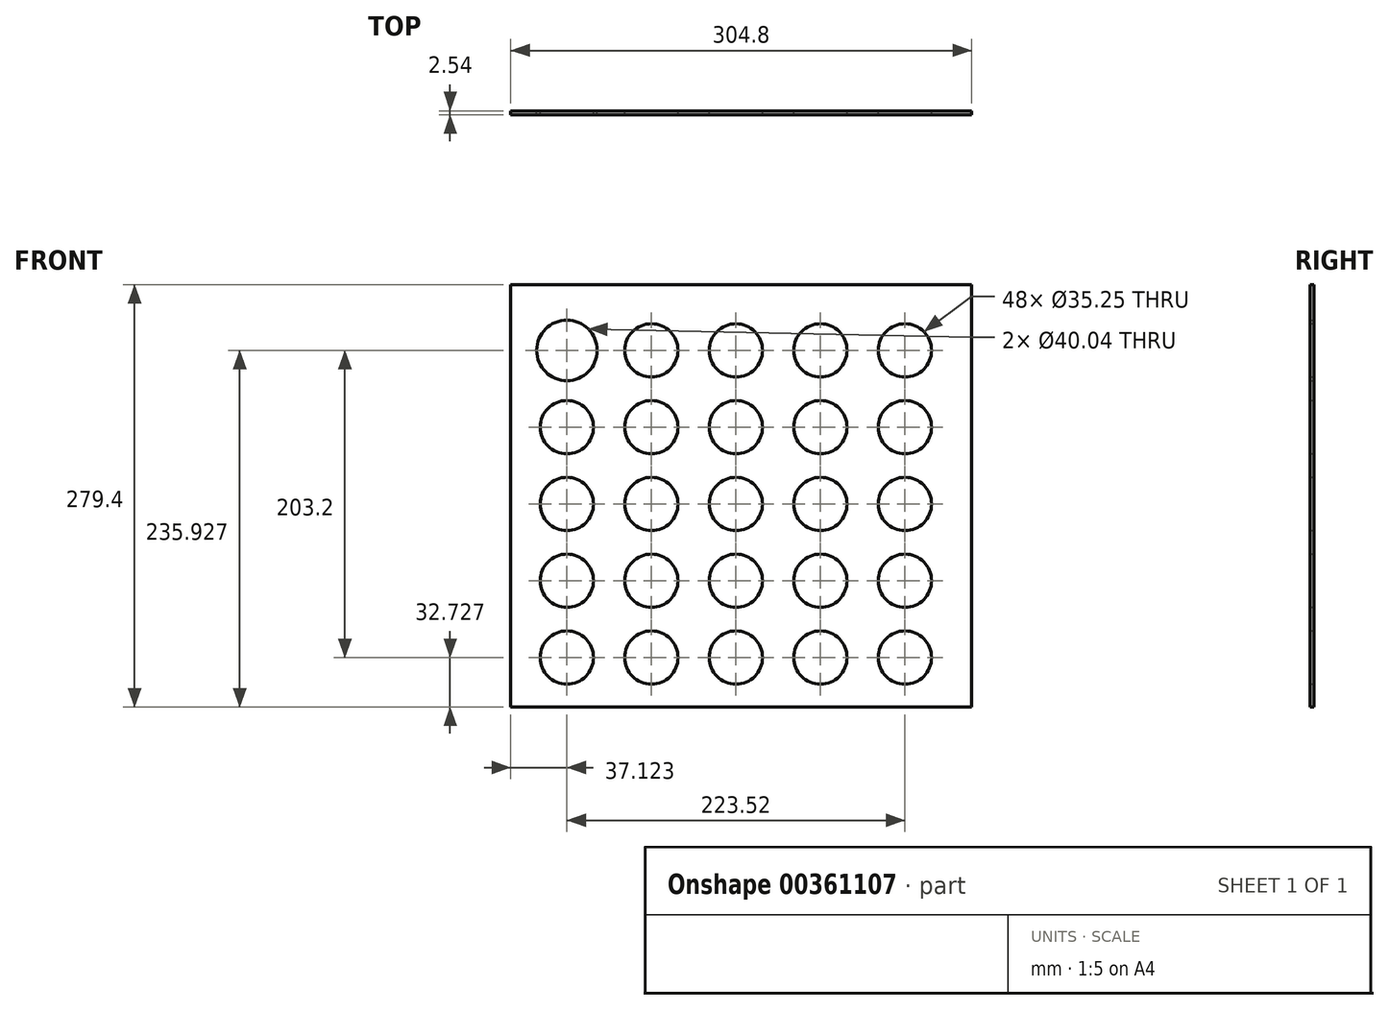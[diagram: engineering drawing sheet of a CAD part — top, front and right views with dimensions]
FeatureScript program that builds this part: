
annotation { "Feature Type Name" : "Feature", "Feature Type Description" : "" }
export const myFeature = defineFeature(function(context is Context, id is Id, definition is map)
    precondition{}
    {
        {
            var Q0;
            Q0=qCreatedBy(makeId("Front.planeOp"),FACE);
            var sketch = newSketch(context, id + "F0", { "sketchPlane" : qUnion([Q0])});
            skLineSegment(sketch, "E0.bottom", {"start": v(-105.95, 167.98) * mm, "end": v(198.85, 167.98) * mm});
            skLineSegment(sketch, "E0.top", {"start": v(-105.95, -111.42) * mm, "end": v(198.85, -111.42) * mm});
            skLineSegment(sketch, "E0.left", {"start": v(-105.95, 167.98) * mm, "end": v(-105.95, -111.42) * mm});
            skLineSegment(sketch, "E0.right", {"start": v(198.85, 167.98) * mm, "end": v(198.85, -111.42) * mm});
            skCircle(sketch, "E1", {"center": v(-68.83, 124.5) * mm, "radius": 20.02 * mm});
            skCircle(sketch, "E2", {"center": v(-68.83, 124.5) * mm, "radius": 17.62 * mm});
            skCircle(sketch, "E3.0.1.0", {"center": v(-68.83, 73.7) * mm, "radius": 17.62 * mm});
            skCircle(sketch, "E3.0.2.0", {"center": v(-68.83, 22.9) * mm, "radius": 17.62 * mm});
            skCircle(sketch, "E3.0.3.0", {"center": v(-68.83, -27.9) * mm, "radius": 17.62 * mm});
            skCircle(sketch, "E3.0.4.0", {"center": v(-68.83, -78.7) * mm, "radius": 17.62 * mm});
            skCircle(sketch, "E3.1.0.0", {"center": v(-12.95, 124.5) * mm, "radius": 17.62 * mm});
            skCircle(sketch, "E3.1.1.0", {"center": v(-12.95, 73.7) * mm, "radius": 17.62 * mm});
            skCircle(sketch, "E3.1.2.0", {"center": v(-12.95, 22.9) * mm, "radius": 17.62 * mm});
            skCircle(sketch, "E3.1.3.0", {"center": v(-12.95, -27.9) * mm, "radius": 17.62 * mm});
            skCircle(sketch, "E3.1.4.0", {"center": v(-12.95, -78.7) * mm, "radius": 17.62 * mm});
            skCircle(sketch, "E3.2.0.0", {"center": v(42.93, 124.5) * mm, "radius": 17.62 * mm});
            skCircle(sketch, "E3.2.1.0", {"center": v(42.93, 73.7) * mm, "radius": 17.62 * mm});
            skCircle(sketch, "E3.2.2.0", {"center": v(42.93, 22.9) * mm, "radius": 17.62 * mm});
            skCircle(sketch, "E3.2.3.0", {"center": v(42.93, -27.9) * mm, "radius": 17.62 * mm});
            skCircle(sketch, "E3.2.4.0", {"center": v(42.93, -78.7) * mm, "radius": 17.62 * mm});
            skCircle(sketch, "E3.3.0.0", {"center": v(98.81, 124.5) * mm, "radius": 17.62 * mm});
            skCircle(sketch, "E3.3.1.0", {"center": v(98.81, 73.7) * mm, "radius": 17.62 * mm});
            skCircle(sketch, "E3.3.2.0", {"center": v(98.81, 22.9) * mm, "radius": 17.62 * mm});
            skCircle(sketch, "E3.3.3.0", {"center": v(98.81, -27.9) * mm, "radius": 17.62 * mm});
            skCircle(sketch, "E3.3.4.0", {"center": v(98.81, -78.7) * mm, "radius": 17.62 * mm});
            skCircle(sketch, "E3.4.0.0", {"center": v(154.7, 124.5) * mm, "radius": 17.62 * mm});
            skCircle(sketch, "E3.4.1.0", {"center": v(154.7, 73.7) * mm, "radius": 17.62 * mm});
            skCircle(sketch, "E3.4.2.0", {"center": v(154.7, 22.9) * mm, "radius": 17.62 * mm});
            skCircle(sketch, "E3.4.3.0", {"center": v(154.7, -27.9) * mm, "radius": 17.62 * mm});
            skCircle(sketch, "E3.4.4.0", {"center": v(154.7, -78.7) * mm, "radius": 17.62 * mm});
            skLineSegment(sketch, "E3.direction1", {"start": v(-68.83, 124.5) * mm, "end": v(-12.95, 124.5) * mm, "construction": true});
            skLineSegment(sketch, "E3.direction2", {"start": v(-68.83, 124.5) * mm, "end": v(-68.83, 73.7) * mm, "construction": true});
            skSolve(sketch);
        }
        {
            var Q0;
            Q0 = qSketchRegion(id + "F0", true);
            extrude(context, id + "F1", {"entities" : qUnion([Q0]), "depth" : 2.54 * mm});
        }
        {
            var Q0;
            Q0 = qSketchRegion(id + "F0", true);
            extrude(context, id + "F2", {"entities" : qUnion([Q0]), "depth" : 0.03 * mm});
        }
    });
